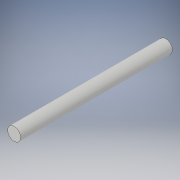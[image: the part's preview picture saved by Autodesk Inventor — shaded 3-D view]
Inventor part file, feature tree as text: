
AUTODESK INVENTOR PART (.ipt)
format: ipt  version: 2019 (Build 230136000, 136)  size: 95,232 bytes
history: native  units: mm
features: sketch x2, other x1, extrude x1
ambient origin geometry x8: Origin, YZ Plane, XZ Plane, XY Plane, X Axis, Y Axis, Z Axis, Center Point
bodies: Body1 (feature_tree)
feature tree (4):
  other  "ソリッド1"
  sketch  "スケッチ1"
  extrude  "押し出し1"  Depth=6.0mm
  sketch  "スケッチ2"
